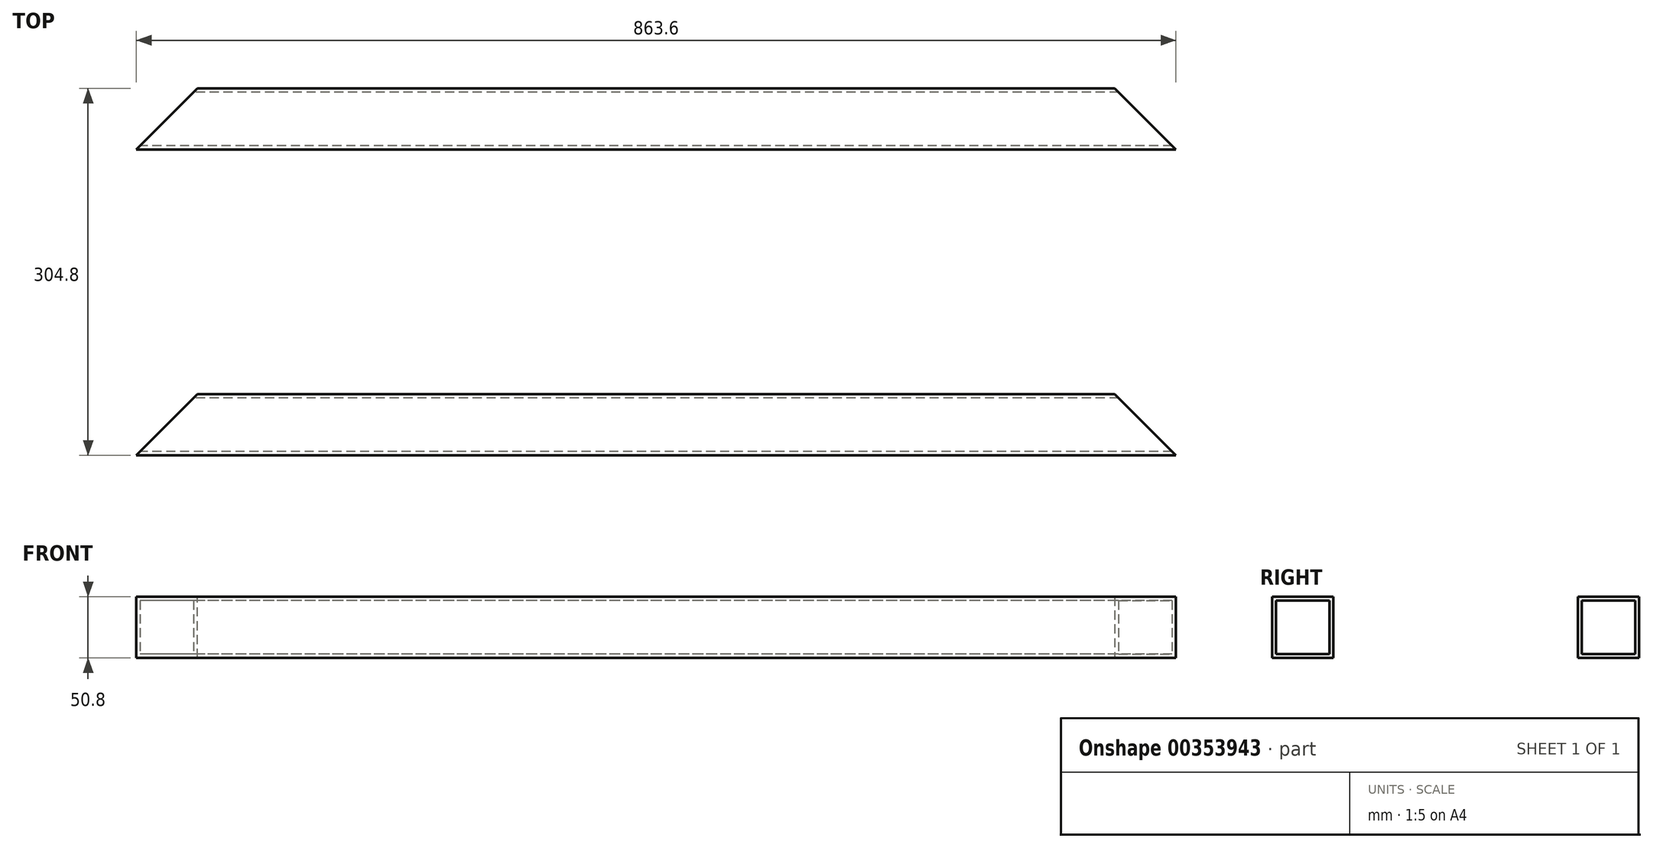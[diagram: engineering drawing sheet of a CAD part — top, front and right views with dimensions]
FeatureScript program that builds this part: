
annotation { "Feature Type Name" : "Feature", "Feature Type Description" : "" }
export const myFeature = defineFeature(function(context is Context, id is Id, definition is map)
    precondition{}
    {
        {
            var Q0;
            Q0=qCreatedBy(makeId("Front.planeOp"),FACE);
            var sketch = newSketch(context, id + "F0", { "sketchPlane" : qUnion([Q0])});
            skLineSegment(sketch, "E0.bottom", {"start": v(431.8, 25.4) * mm, "end": v(-431.8, 25.4) * mm});
            skLineSegment(sketch, "E0.top", {"start": v(431.8, -25.4) * mm, "end": v(-431.8, -25.4) * mm});
            skLineSegment(sketch, "E0.left", {"start": v(431.8, 25.4) * mm, "end": v(431.8, -25.4) * mm});
            skLineSegment(sketch, "E0.right", {"start": v(-431.8, 25.4) * mm, "end": v(-431.8, -25.4) * mm});
            skPoint(sketch, "E0.middle", {"position": v(0, 0) * mm});
            skSolve(sketch);
        }
        {
            var Q0;
            Q0=qSketchRegion(id+"F0",true);
            extrude(context, id + "F1", {"entities" : qUnion([Q0]), "depth" : 50.8 * mm});
        }
        {
            var Q0;
            Q0=makeQuery(id+"F1.opExtrude","SWEPT_FACE",FACE,{"disambiguationData":[OSD([sQuery(id+"F0.wireOp",EDGE,"E0.right")])]});
            var sketch = newSketch(context, id + "F2", { "sketchPlane" : qUnion([Q0])});
            skLineSegment(sketch, "E1.bottom", {"start": v(47.63, -22.23) * mm, "end": v(3.18, -22.23) * mm});
            skLineSegment(sketch, "E1.top", {"start": v(47.63, 22.23) * mm, "end": v(3.18, 22.23) * mm});
            skLineSegment(sketch, "E1.left", {"start": v(47.63, -22.23) * mm, "end": v(47.63, 22.23) * mm});
            skLineSegment(sketch, "E1.right", {"start": v(3.18, -22.23) * mm, "end": v(3.17, 22.23) * mm});
            skPoint(sketch, "E1.middle", {"position": v(25.4, 0) * mm});
            skSolve(sketch);
        }
        {
            var Q0;
            Q0=qSketchRegion(id+"F2",true);
            extrude(context, id + "F3", {"entities" : qUnion([Q0]), "operationType" : NewBodyOperationType.REMOVE, "endBound" : BoundingType.THROUGH_ALL, "oppositeDirection" : true, "depth" : 25.4 * mm});
        }
        {
            var Q0;
            Q0=makeQuery(id+"F1.opExtrude","CAP_EDGE",EDGE,{"disambiguationData":[OSD([sQuery(id+"F0.wireOp",EDGE,"E0.left")])],"isStart":true});
            var Q1;
            Q1=makeQuery(id+"F1.opExtrude","CAP_EDGE",EDGE,{"disambiguationData":[OSD([sQuery(id+"F0.wireOp",EDGE,"E0.right")])],"isStart":true});
            chamfer(context, id + "F4", {"entities" : qUnion([Q0, Q1]), "width" : 50.8 * mm, "tangentPropagation" : true});
        }
        {
            var Q0;
            Q0=makeQuery(id+"F1.opExtrude","SWEPT_BODY",BODY,{"disambiguationData":[OSD([sQuery(id+"F0.wireOp",EDGE,"E0.bottom"),sQuery(id+"F0.wireOp",EDGE,"E0.top"),sQuery(id+"F0.wireOp",EDGE,"E0.left"),sQuery(id+"F0.wireOp",EDGE,"E0.right")])]});
            transform(context, id + "F5", {"entities" : qUnion([Q0]), "transformType" : TransformType.TRANSLATION_3D, "dx" : 0 * mm, "dy" : 254 * mm, "dz" : 0 * mm, "makeCopy" : true});
        }
    });
